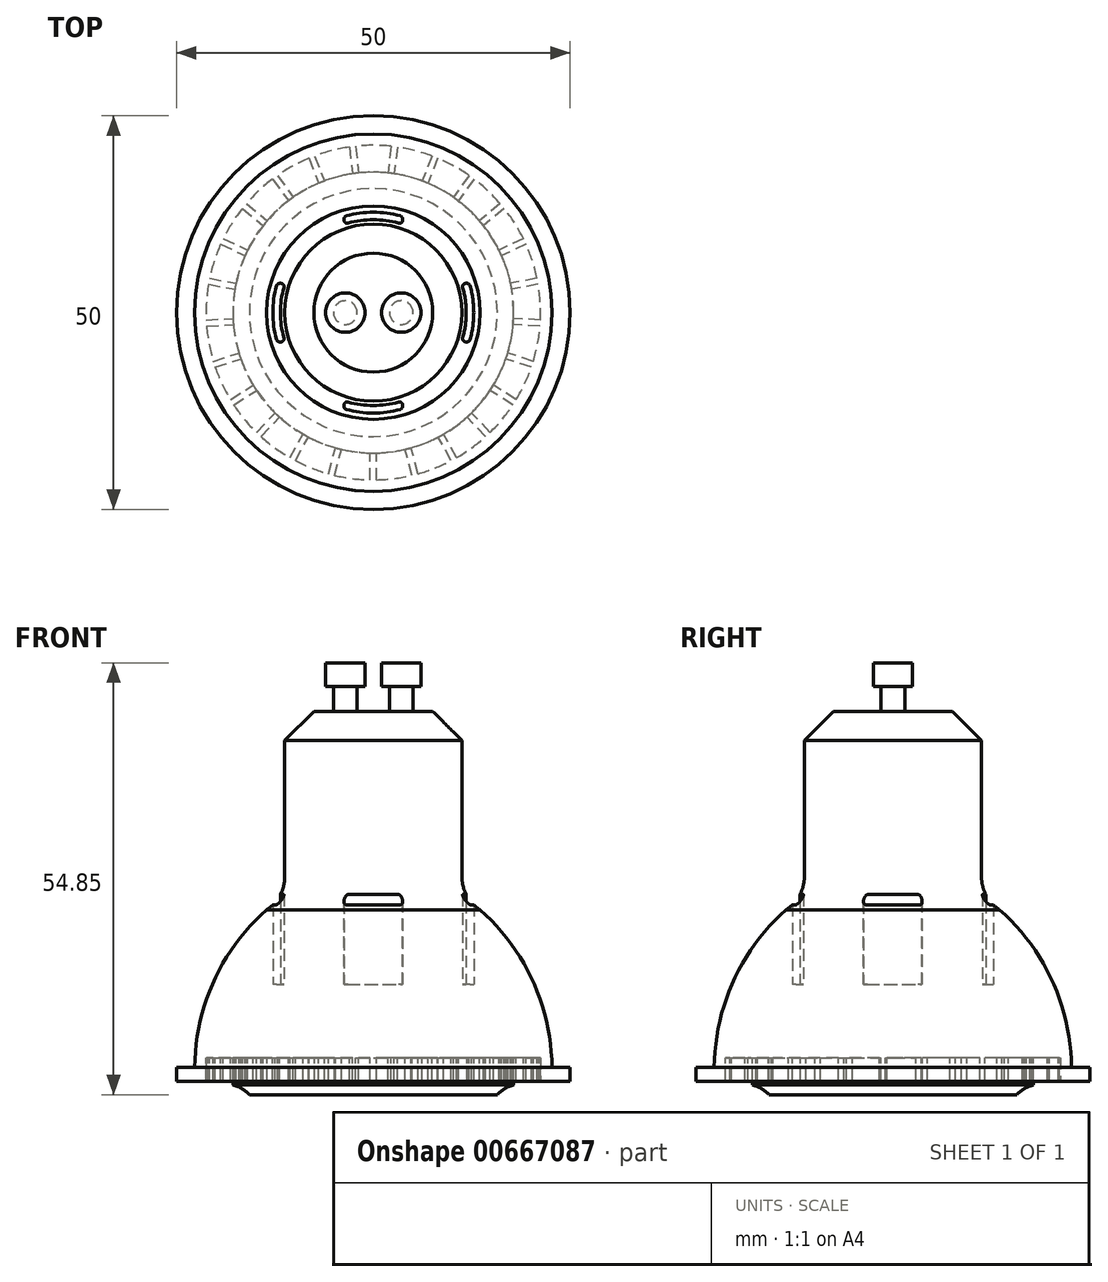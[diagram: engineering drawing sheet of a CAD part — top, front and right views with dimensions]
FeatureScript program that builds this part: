
annotation { "Feature Type Name" : "Feature", "Feature Type Description" : "" }
export const myFeature = defineFeature(function(context is Context, id is Id, definition is map)
    precondition{}
    {
        {
            var Q0;
            Q0=qCreatedBy(makeId("Front.planeOp"),FACE);
            var sketch = newSketch(context, id + "F0", { "sketchPlane" : qUnion([Q0])});
            skLineSegment(sketch, "E0", {"start": v(0, 34.68) * mm, "end": v(0, -12.32) * mm});
            skLineSegment(sketch, "E1", {"start": v(0, -12.32) * mm, "end": v(-25, -12.32) * mm});
            skLineSegment(sketch, "E2", {"start": v(-25, -12.32) * mm, "end": v(-25, -10.52) * mm});
            skLineSegment(sketch, "E3", {"start": v(-25, -10.52) * mm, "end": v(-22.7, -10.52) * mm});
            skLineSegment(sketch, "E4", {"start": v(0, 34.68) * mm, "end": v(-7.55, 34.68) * mm});
            skLineSegment(sketch, "E5", {"start": v(-7.55, 34.68) * mm, "end": v(-11.25, 30.98) * mm});
            skLineSegment(sketch, "E6", {"start": v(-11.25, 30.98) * mm, "end": v(-11.25, 13.7) * mm});
            skArc(sketch, "E7", {"start": v(-13.56, 9.48) * mm, "mid": v(-11.86, 11.3) * mm, "end": v(-11.25, 13.7) * mm});
            skArc(sketch, "E8", {"start": v(-13.56, 9.48) * mm, "mid": v(-20.24, 0.44) * mm, "end": v(-22.7, -10.52) * mm});
            skSolve(sketch);
        }
        {
            var Q0;
            Q0=makeQuery(id+"F0.imprint","IMPRINT",FACE,{"disambiguationData":[TD([[makeQuery(id+"F0.imprint","IMPRINT",EDGE,{"derivedFrom":sQuery(id+"F0.wireOp",EDGE,"E0")}),-1.0]])]});
            var Q1;
            Q1=sQuery(id+"F0.wireOp",EDGE,"E0");
            revolve(context, id + "F1", {"entities" : qUnion([Q0]), "axis" : qUnion([Q1]), "revolveType" : RevolveType.FULL});
        }
        {
            var Q0;
            Q0=makeQuery(id+"F1.opRevolve","SWEPT_FACE",FACE,{"disambiguationData":[OSD([sQuery(id+"F0.wireOp",EDGE,"E4")])]});
            var sketch = newSketch(context, id + "F2", { "sketchPlane" : qUnion([Q0])});
            skCircle(sketch, "E9", {"center": v(-3.55, 0) * mm, "radius": 1.5 * mm});
            skLineSegment(sketch, "E10", {"start": v(0, 1.94) * mm, "end": v(0, -1.69) * mm});
            skCircle(sketch, "E11.MirrorC", {"center": v(3.55, 0) * mm, "radius": 1.5 * mm});
            skSolve(sketch);
        }
        {
            var Q0;
            Q0=qSketchRegion(id+"F2",true);
            extrude(context, id + "F3", {"entities" : qUnion([Q0]), "operationType" : NewBodyOperationType.ADD, "depth" : 3.15 * mm, "offsetDistance" : 25 * mm});
        }
        {
            var Q0;
            Q0=makeQuery(id+"F3.opExtrude","CAP_FACE",FACE,{"disambiguationData":[OSD([sQuery(id+"F2.wireOp",EDGE,"E9")])],"isStart":false});
            var sketch = newSketch(context, id + "F4", { "sketchPlane" : qUnion([Q0])});
            skCircle(sketch, "E12", {"center": v(-3.55, 0) * mm, "radius": 2.5 * mm});
            skLineSegment(sketch, "E13", {"start": v(0, 3.4) * mm, "end": v(0, -2.9) * mm});
            skCircle(sketch, "E14.MirrorC", {"center": v(3.55, 0) * mm, "radius": 2.5 * mm});
            skSolve(sketch);
        }
        {
            var Q0;
            Q0=qSketchRegion(id+"F4",true);
            extrude(context, id + "F5", {"entities" : qUnion([Q0]), "operationType" : NewBodyOperationType.ADD, "depth" : 3 * mm, "offsetDistance" : 25 * mm});
        }
        {
            var Q0;
            Q0=qCreatedBy(makeId("Front.planeOp"),FACE);
            var sketch = newSketch(context, id + "F6", { "sketchPlane" : qUnion([Q0])});
            skLineSegment(sketch, "E15", {"start": v(0, -12.32) * mm, "end": v(0, -14.02) * mm});
            skLineSegment(sketch, "E16", {"start": v(0, -14.02) * mm, "end": v(-15.75, -14.02) * mm});
            skArc(sketch, "E17", {"start": v(-15.75, -14.02) * mm, "mid": v(-16.7, -13.24) * mm, "end": v(-17.84, -12.8) * mm});
            skLineSegment(sketch, "E18", {"start": v(-17.84, -12.8) * mm, "end": v(-17.84, -12.32) * mm});
            skLineSegment(sketch, "E19", {"start": v(-17.84, -12.32) * mm, "end": v(0, -12.32) * mm});
            skSolve(sketch);
        }
        {
            var Q0;
            Q0=qSketchRegion(id+"F6",true);
            var Q1;
            Q1=sQuery(id+"F6.wireOp",EDGE,"E15");
            revolve(context, id + "F7", {"operationType" : NewBodyOperationType.ADD, "entities" : qUnion([Q0]), "axis" : qUnion([Q1]), "revolveType" : RevolveType.FULL});
        }
        {
            var Q0;
            Q0=makeQuery(id+"F1.opRevolve","SWEPT_FACE",FACE,{"disambiguationData":[OSD([sQuery(id+"F0.wireOp",EDGE,"E1")])]});
            var sketch = newSketch(context, id + "F8", { "sketchPlane" : qUnion([Q0])});
            skCircle(sketch, "E20", {"center": v(0, 0) * mm, "radius": 17.84 * mm});
            skCircle(sketch, "E21", {"center": v(0, 0) * mm, "radius": 21.25 * mm});
            skSolve(sketch);
        }
        {
            var Q0;
            Q0=qSketchRegion(id+"F8",true);
            extrude(context, id + "F9", {"entities" : qUnion([Q0]), "operationType" : NewBodyOperationType.REMOVE, "oppositeDirection" : true, "depth" : 3 * mm, "offsetDistance" : 25 * mm});
        }
        {
            var Q0;
            Q0=makeQuery(id+"F9.boolean.opBoolean","COPY",FACE,{"derivedFrom":makeQuery(id+"F9.opExtrude","CAP_FACE",FACE,{"disambiguationData":[OSD([sQuery(id+"F8.wireOp",EDGE,"E20"),sQuery(id+"F8.wireOp",EDGE,"E21")])],"isStart":false})});
            var sketch = newSketch(context, id + "F10", { "sketchPlane" : qUnion([Q0])});
            skLineSegment(sketch, "E22.left", {"start": v(-0.4, 21.25) * mm, "end": v(-0.4, 17.83) * mm});
            skLineSegment(sketch, "E22.right", {"start": v(0.4, 21.25) * mm, "end": v(0.4, 17.83) * mm});
            skArc(sketch, "E23", {"start": v(0.4, 17.83) * mm, "mid": v(0, 17.84) * mm, "end": v(-0.39, 17.83) * mm});
            skArc(sketch, "E24", {"start": v(0.39, 21.25) * mm, "mid": v(0, 21.25) * mm, "end": v(-0.39, 21.25) * mm});
            skArc(sketch, "E25.1.0", {"start": v(-4.9, 20.68) * mm, "mid": v(-5.28, 20.58) * mm, "end": v(-5.66, 20.48) * mm});
            skLineSegment(sketch, "E25.1.1", {"start": v(-4.9, 20.68) * mm, "end": v(-4.06, 17.37) * mm});
            skLineSegment(sketch, "E25.1.2", {"start": v(-5.66, 20.48) * mm, "end": v(-4.81, 17.17) * mm});
            skArc(sketch, "E25.1.3", {"start": v(-4.06, 17.37) * mm, "mid": v(-4.44, 17.28) * mm, "end": v(-4.81, 17.17) * mm});
            skArc(sketch, "E25.2.0", {"start": v(-9.9, 18.8) * mm, "mid": v(-10.24, 18.62) * mm, "end": v(-10.58, 18.43) * mm});
            skLineSegment(sketch, "E25.2.1", {"start": v(-9.9, 18.8) * mm, "end": v(-8.25, 15.81) * mm});
            skLineSegment(sketch, "E25.2.2", {"start": v(-10.58, 18.43) * mm, "end": v(-8.93, 15.44) * mm});
            skArc(sketch, "E25.2.3", {"start": v(-8.25, 15.81) * mm, "mid": v(-8.6, 15.63) * mm, "end": v(-8.93, 15.44) * mm});
            skArc(sketch, "E26.3.3.0", {"start": v(-14.26, 15.75) * mm, "mid": v(-14.55, 15.5) * mm, "end": v(-14.83, 15.22) * mm});
            skLineSegment(sketch, "E26.4.3.0", {"start": v(-14.26, 15.75) * mm, "end": v(-11.92, 13.27) * mm});
            skLineSegment(sketch, "E26.7.3.0", {"start": v(-14.83, 15.22) * mm, "end": v(-12.5, 12.73) * mm});
            skArc(sketch, "E26.10.3.0", {"start": v(-11.92, 13.27) * mm, "mid": v(-12.2, 13) * mm, "end": v(-12.5, 12.73) * mm});
            skArc(sketch, "E26.3.4.0", {"start": v(-17.73, 11.71) * mm, "mid": v(-17.94, 11.39) * mm, "end": v(-18.15, 11.06) * mm});
            skLineSegment(sketch, "E26.4.4.0", {"start": v(-17.73, 11.71) * mm, "end": v(-14.85, 9.88) * mm});
            skLineSegment(sketch, "E26.7.4.0", {"start": v(-18.15, 11.06) * mm, "end": v(-15.27, 9.23) * mm});
            skArc(sketch, "E26.10.4.0", {"start": v(-14.85, 9.88) * mm, "mid": v(-15.06, 9.56) * mm, "end": v(-15.27, 9.23) * mm});
            skArc(sketch, "E26.3.5.0", {"start": v(-20.09, 6.94) * mm, "mid": v(-20.2, 6.57) * mm, "end": v(-20.33, 6.2) * mm});
            skLineSegment(sketch, "E26.4.5.0", {"start": v(-20.09, 6.94) * mm, "end": v(-16.84, 5.88) * mm});
            skLineSegment(sketch, "E26.7.5.0", {"start": v(-20.33, 6.2) * mm, "end": v(-17.08, 5.14) * mm});
            skArc(sketch, "E26.10.5.0", {"start": v(-16.84, 5.88) * mm, "mid": v(-16.96, 5.51) * mm, "end": v(-17.08, 5.14) * mm});
            skArc(sketch, "E26.3.6.0", {"start": v(-21.18, 1.72) * mm, "mid": v(-21.2, 1.33) * mm, "end": v(-21.23, 0.94) * mm});
            skLineSegment(sketch, "E26.4.6.0", {"start": v(-21.18, 1.72) * mm, "end": v(-17.77, 1.5) * mm});
            skLineSegment(sketch, "E26.7.6.0", {"start": v(-21.23, 0.94) * mm, "end": v(-17.82, 0.73) * mm});
            skArc(sketch, "E26.10.6.0", {"start": v(-17.77, 1.5) * mm, "mid": v(-17.8, 1.12) * mm, "end": v(-17.82, 0.73) * mm});
            skArc(sketch, "E26.3.7.0", {"start": v(-20.94, -3.6) * mm, "mid": v(-20.87, -3.98) * mm, "end": v(-20.8, -4.36) * mm});
            skLineSegment(sketch, "E26.4.7.0", {"start": v(-20.94, -3.6) * mm, "end": v(-17.59, -2.96) * mm});
            skLineSegment(sketch, "E26.7.7.0", {"start": v(-20.8, -4.36) * mm, "end": v(-17.44, -3.72) * mm});
            skArc(sketch, "E26.10.7.0", {"start": v(-17.59, -2.96) * mm, "mid": v(-17.52, -3.34) * mm, "end": v(-17.44, -3.72) * mm});
            skArc(sketch, "E26.3.8.0", {"start": v(-19.4, -8.7) * mm, "mid": v(-19.23, -9.05) * mm, "end": v(-19.06, -9.4) * mm});
            skLineSegment(sketch, "E26.4.8.0", {"start": v(-19.4, -8.7) * mm, "end": v(-16.3, -7.24) * mm});
            skLineSegment(sketch, "E26.7.8.0", {"start": v(-19.06, -9.4) * mm, "end": v(-15.97, -7.95) * mm});
            skArc(sketch, "E26.10.8.0", {"start": v(-16.3, -7.24) * mm, "mid": v(-16.14, -7.6) * mm, "end": v(-15.97, -7.95) * mm});
            skArc(sketch, "E26.3.9.0", {"start": v(-16.62, -13.24) * mm, "mid": v(-16.37, -13.55) * mm, "end": v(-16.12, -13.84) * mm});
            skLineSegment(sketch, "E26.4.9.0", {"start": v(-16.62, -13.24) * mm, "end": v(-13.99, -11.07) * mm});
            skLineSegment(sketch, "E26.7.9.0", {"start": v(-16.12, -13.84) * mm, "end": v(-13.5, -11.67) * mm});
            skArc(sketch, "E26.10.9.0", {"start": v(-13.99, -11.07) * mm, "mid": v(-13.74, -11.37) * mm, "end": v(-13.5, -11.67) * mm});
            skArc(sketch, "E26.3.10.0", {"start": v(-12.8, -16.96) * mm, "mid": v(-12.5, -17.2) * mm, "end": v(-12.17, -17.42) * mm});
            skLineSegment(sketch, "E26.4.10.0", {"start": v(-12.8, -16.96) * mm, "end": v(-10.8, -14.2) * mm});
            skLineSegment(sketch, "E26.7.10.0", {"start": v(-12.17, -17.42) * mm, "end": v(-10.17, -14.66) * mm});
            skArc(sketch, "E26.10.10.0", {"start": v(-10.8, -14.2) * mm, "mid": v(-10.48, -14.43) * mm, "end": v(-10.17, -14.66) * mm});
            skArc(sketch, "E26.3.11.0", {"start": v(-8.18, -19.61) * mm, "mid": v(-7.82, -19.76) * mm, "end": v(-7.46, -19.9) * mm});
            skLineSegment(sketch, "E26.4.11.0", {"start": v(-8.18, -19.61) * mm, "end": v(-6.93, -16.44) * mm});
            skLineSegment(sketch, "E26.7.11.0", {"start": v(-7.46, -19.9) * mm, "end": v(-6.2, -16.72) * mm});
            skArc(sketch, "E26.10.11.0", {"start": v(-6.93, -16.44) * mm, "mid": v(-6.57, -16.58) * mm, "end": v(-6.2, -16.72) * mm});
            skArc(sketch, "E26.3.12.0", {"start": v(-3.05, -21.03) * mm, "mid": v(-2.66, -21.08) * mm, "end": v(-2.28, -21.13) * mm});
            skLineSegment(sketch, "E26.4.12.0", {"start": v(-3.05, -21.03) * mm, "end": v(-2.62, -17.64) * mm});
            skLineSegment(sketch, "E26.7.12.0", {"start": v(-2.28, -21.13) * mm, "end": v(-1.85, -17.74) * mm});
            skArc(sketch, "E26.10.12.0", {"start": v(-2.62, -17.64) * mm, "mid": v(-2.24, -17.7) * mm, "end": v(-1.85, -17.74) * mm});
            skArc(sketch, "E26.3.13.0", {"start": v(2.28, -21.13) * mm, "mid": v(2.66, -21.08) * mm, "end": v(3.05, -21.03) * mm});
            skLineSegment(sketch, "E26.4.13.0", {"start": v(2.28, -21.13) * mm, "end": v(1.85, -17.74) * mm});
            skLineSegment(sketch, "E26.7.13.0", {"start": v(3.05, -21.03) * mm, "end": v(2.62, -17.64) * mm});
            skArc(sketch, "E26.10.13.0", {"start": v(1.85, -17.74) * mm, "mid": v(2.24, -17.7) * mm, "end": v(2.62, -17.64) * mm});
            skArc(sketch, "E26.3.14.0", {"start": v(7.46, -19.9) * mm, "mid": v(7.82, -19.76) * mm, "end": v(8.18, -19.61) * mm});
            skLineSegment(sketch, "E26.4.14.0", {"start": v(7.46, -19.9) * mm, "end": v(6.2, -16.72) * mm});
            skLineSegment(sketch, "E26.7.14.0", {"start": v(8.18, -19.61) * mm, "end": v(6.93, -16.44) * mm});
            skArc(sketch, "E26.10.14.0", {"start": v(6.2, -16.72) * mm, "mid": v(6.57, -16.58) * mm, "end": v(6.93, -16.44) * mm});
            skArc(sketch, "E26.3.15.0", {"start": v(12.17, -17.42) * mm, "mid": v(12.5, -17.2) * mm, "end": v(12.8, -16.96) * mm});
            skLineSegment(sketch, "E26.4.15.0", {"start": v(12.17, -17.42) * mm, "end": v(10.17, -14.66) * mm});
            skLineSegment(sketch, "E26.7.15.0", {"start": v(12.8, -16.96) * mm, "end": v(10.8, -14.2) * mm});
            skArc(sketch, "E26.10.15.0", {"start": v(10.17, -14.66) * mm, "mid": v(10.48, -14.43) * mm, "end": v(10.8, -14.2) * mm});
            skArc(sketch, "E26.3.16.0", {"start": v(16.12, -13.84) * mm, "mid": v(16.37, -13.55) * mm, "end": v(16.62, -13.24) * mm});
            skLineSegment(sketch, "E26.4.16.0", {"start": v(16.12, -13.84) * mm, "end": v(13.5, -11.67) * mm});
            skLineSegment(sketch, "E26.7.16.0", {"start": v(16.62, -13.24) * mm, "end": v(13.99, -11.07) * mm});
            skArc(sketch, "E26.10.16.0", {"start": v(13.5, -11.67) * mm, "mid": v(13.74, -11.37) * mm, "end": v(13.99, -11.07) * mm});
            skArc(sketch, "E26.3.17.0", {"start": v(19.06, -9.4) * mm, "mid": v(19.23, -9.05) * mm, "end": v(19.4, -8.7) * mm});
            skLineSegment(sketch, "E26.4.17.0", {"start": v(19.06, -9.4) * mm, "end": v(15.97, -7.95) * mm});
            skLineSegment(sketch, "E26.7.17.0", {"start": v(19.4, -8.7) * mm, "end": v(16.3, -7.24) * mm});
            skArc(sketch, "E26.10.17.0", {"start": v(15.97, -7.95) * mm, "mid": v(16.14, -7.6) * mm, "end": v(16.3, -7.24) * mm});
            skArc(sketch, "E26.3.18.0", {"start": v(20.8, -4.36) * mm, "mid": v(20.87, -3.98) * mm, "end": v(20.94, -3.6) * mm});
            skLineSegment(sketch, "E26.4.18.0", {"start": v(20.8, -4.36) * mm, "end": v(17.44, -3.72) * mm});
            skLineSegment(sketch, "E26.7.18.0", {"start": v(20.94, -3.6) * mm, "end": v(17.59, -2.96) * mm});
            skArc(sketch, "E26.10.18.0", {"start": v(17.44, -3.72) * mm, "mid": v(17.52, -3.34) * mm, "end": v(17.59, -2.96) * mm});
            skArc(sketch, "E26.3.19.0", {"start": v(21.23, 0.94) * mm, "mid": v(21.2, 1.33) * mm, "end": v(21.18, 1.72) * mm});
            skLineSegment(sketch, "E26.4.19.0", {"start": v(21.23, 0.94) * mm, "end": v(17.82, 0.73) * mm});
            skLineSegment(sketch, "E26.7.19.0", {"start": v(21.18, 1.72) * mm, "end": v(17.77, 1.5) * mm});
            skArc(sketch, "E26.10.19.0", {"start": v(17.82, 0.73) * mm, "mid": v(17.8, 1.12) * mm, "end": v(17.77, 1.5) * mm});
            skArc(sketch, "E26.3.20.0", {"start": v(20.33, 6.2) * mm, "mid": v(20.2, 6.57) * mm, "end": v(20.09, 6.94) * mm});
            skLineSegment(sketch, "E26.4.20.0", {"start": v(20.33, 6.2) * mm, "end": v(17.08, 5.14) * mm});
            skLineSegment(sketch, "E26.7.20.0", {"start": v(20.09, 6.94) * mm, "end": v(16.84, 5.88) * mm});
            skArc(sketch, "E26.10.20.0", {"start": v(17.08, 5.14) * mm, "mid": v(16.96, 5.51) * mm, "end": v(16.84, 5.88) * mm});
            skArc(sketch, "E26.3.21.0", {"start": v(18.15, 11.06) * mm, "mid": v(17.94, 11.39) * mm, "end": v(17.73, 11.71) * mm});
            skLineSegment(sketch, "E26.4.21.0", {"start": v(18.15, 11.06) * mm, "end": v(15.27, 9.23) * mm});
            skLineSegment(sketch, "E26.7.21.0", {"start": v(17.73, 11.71) * mm, "end": v(14.85, 9.88) * mm});
            skArc(sketch, "E26.10.21.0", {"start": v(15.27, 9.23) * mm, "mid": v(15.06, 9.56) * mm, "end": v(14.85, 9.88) * mm});
            skArc(sketch, "E26.3.22.0", {"start": v(14.83, 15.22) * mm, "mid": v(14.55, 15.5) * mm, "end": v(14.26, 15.75) * mm});
            skLineSegment(sketch, "E26.4.22.0", {"start": v(14.83, 15.22) * mm, "end": v(12.5, 12.73) * mm});
            skLineSegment(sketch, "E26.7.22.0", {"start": v(14.26, 15.75) * mm, "end": v(11.92, 13.27) * mm});
            skArc(sketch, "E26.10.22.0", {"start": v(12.5, 12.73) * mm, "mid": v(12.2, 13) * mm, "end": v(11.92, 13.27) * mm});
            skArc(sketch, "E26.3.23.0", {"start": v(10.58, 18.43) * mm, "mid": v(10.24, 18.62) * mm, "end": v(9.9, 18.8) * mm});
            skLineSegment(sketch, "E26.4.23.0", {"start": v(10.58, 18.43) * mm, "end": v(8.93, 15.44) * mm});
            skLineSegment(sketch, "E26.7.23.0", {"start": v(9.9, 18.8) * mm, "end": v(8.25, 15.81) * mm});
            skArc(sketch, "E26.10.23.0", {"start": v(8.93, 15.44) * mm, "mid": v(8.6, 15.63) * mm, "end": v(8.25, 15.81) * mm});
            skArc(sketch, "E26.3.24.0", {"start": v(5.66, 20.48) * mm, "mid": v(5.28, 20.58) * mm, "end": v(4.9, 20.68) * mm});
            skLineSegment(sketch, "E26.4.24.0", {"start": v(5.66, 20.48) * mm, "end": v(4.81, 17.17) * mm});
            skLineSegment(sketch, "E26.7.24.0", {"start": v(4.9, 20.68) * mm, "end": v(4.06, 17.37) * mm});
            skArc(sketch, "E26.10.24.0", {"start": v(4.81, 17.17) * mm, "mid": v(4.44, 17.28) * mm, "end": v(4.06, 17.37) * mm});
            skSolve(sketch);
        }
        {
            var Q0;
            Q0=qSketchRegion(id+"F10",true);
            var Q1;
            Q1=makeQuery(id+"F1.opRevolve","SWEPT_FACE",FACE,{"disambiguationData":[OSD([sQuery(id+"F0.wireOp",EDGE,"E1")])]});
            extrude(context, id + "F11", {"entities" : qUnion([Q0]), "operationType" : NewBodyOperationType.ADD, "endBound" : BoundingType.UP_TO_SURFACE, "depth" : 25 * mm, "endBoundEntityFace" : qUnion([Q1]), "offsetDistance" : 25 * mm});
        }
        {
            var Q0;
            Q0=qCreatedBy(makeId("Top.planeOp"),FACE);
            var sketch = newSketch(context, id + "F12", { "sketchPlane" : qUnion([Q0])});
            skArc(sketch, "E27", {"start": v(3.72, 11.2) * mm, "mid": v(0, 11.8) * mm, "end": v(-3.72, 11.2) * mm});
            skArc(sketch, "E28", {"start": v(3.72, 12.2) * mm, "mid": v(0, 12.76) * mm, "end": v(-3.72, 12.2) * mm});
            skLineSegment(sketch, "E29", {"start": v(-3.72, 12.2) * mm, "end": v(-3.72, 11.2) * mm});
            skLineSegment(sketch, "E30.MirrorCS", {"start": v(3.72, 12.2) * mm, "end": v(3.72, 11.2) * mm});
            skPoint(sketch, "E31.start.orphan", {"position": v(0, 15.57) * mm});
            skArc(sketch, "E32.1.0", {"start": v(-12.2, 3.72) * mm, "mid": v(-12.76, 0) * mm, "end": v(-12.2, -3.72) * mm});
            skLineSegment(sketch, "E32.1.1", {"start": v(-12.2, -3.72) * mm, "end": v(-11.2, -3.72) * mm});
            skArc(sketch, "E32.1.2", {"start": v(-11.2, 3.72) * mm, "mid": v(-11.8, 0) * mm, "end": v(-11.2, -3.72) * mm});
            skLineSegment(sketch, "E32.1.3", {"start": v(-12.2, 3.72) * mm, "end": v(-11.2, 3.72) * mm});
            skArc(sketch, "E32.2.0", {"start": v(-3.72, -12.2) * mm, "mid": v(0, -12.76) * mm, "end": v(3.72, -12.2) * mm});
            skLineSegment(sketch, "E32.2.1", {"start": v(3.72, -12.2) * mm, "end": v(3.72, -11.2) * mm});
            skArc(sketch, "E32.2.2", {"start": v(-3.72, -11.2) * mm, "mid": v(0, -11.8) * mm, "end": v(3.72, -11.2) * mm});
            skLineSegment(sketch, "E32.2.3", {"start": v(-3.72, -12.2) * mm, "end": v(-3.72, -11.2) * mm});
            skArc(sketch, "E32.3.0", {"start": v(12.2, -3.72) * mm, "mid": v(12.76, 0) * mm, "end": v(12.2, 3.72) * mm});
            skLineSegment(sketch, "E32.3.1", {"start": v(12.2, 3.72) * mm, "end": v(11.2, 3.72) * mm});
            skArc(sketch, "E32.3.2", {"start": v(11.2, -3.72) * mm, "mid": v(11.8, 0) * mm, "end": v(11.2, 3.72) * mm});
            skLineSegment(sketch, "E32.3.3", {"start": v(12.2, -3.72) * mm, "end": v(11.2, -3.72) * mm});
            skSolve(sketch);
        }
        {
            var Q0;
            Q0=qSketchRegion(id+"F12",true);
            extrude(context, id + "F13", {"entities" : qUnion([Q0]), "operationType" : NewBodyOperationType.REMOVE, "depth" : 22.5 * mm, "offsetDistance" : 25 * mm});
        }
        {
            var Q0;
            Q0=makeQuery(id+"F13.boolean.opBoolean","COPY",EDGE,{"derivedFrom":makeQuery(id+"F13.opExtrude","SWEPT_EDGE",EDGE,{"disambiguationData":[OSD([sQuery(id+"F12.wireOp",EDGE,"E27"),sQuery(id+"F12.wireOp",EDGE,"E29")])]})});
            var Q1;
            Q1=makeQuery(id+"F13.boolean.opBoolean","COPY",EDGE,{"derivedFrom":makeQuery(id+"F13.opExtrude","SWEPT_EDGE",EDGE,{"disambiguationData":[OSD([sQuery(id+"F12.wireOp",EDGE,"E28"),sQuery(id+"F12.wireOp",EDGE,"E29")])]})});
            var Q2;
            Q2=makeQuery(id+"F13.boolean.opBoolean","COPY",EDGE,{"derivedFrom":makeQuery(id+"F13.opExtrude","SWEPT_EDGE",EDGE,{"disambiguationData":[OSD([sQuery(id+"F12.wireOp",EDGE,"E27"),sQuery(id+"F12.wireOp",EDGE,"E30.MirrorCS")])]})});
            var Q3;
            Q3=makeQuery(id+"F13.boolean.opBoolean","COPY",EDGE,{"derivedFrom":makeQuery(id+"F13.opExtrude","SWEPT_EDGE",EDGE,{"disambiguationData":[OSD([sQuery(id+"F12.wireOp",EDGE,"E28"),sQuery(id+"F12.wireOp",EDGE,"E30.MirrorCS")])]})});
            var Q4;
            Q4=makeQuery(id+"F13.boolean.opBoolean","COPY",EDGE,{"derivedFrom":makeQuery(id+"F13.opExtrude","SWEPT_EDGE",EDGE,{"disambiguationData":[OSD([sQuery(id+"F12.wireOp",EDGE,"E32.1.0"),sQuery(id+"F12.wireOp",EDGE,"E32.1.3")])]})});
            var Q5;
            Q5=makeQuery(id+"F13.boolean.opBoolean","COPY",EDGE,{"derivedFrom":makeQuery(id+"F13.opExtrude","SWEPT_EDGE",EDGE,{"disambiguationData":[OSD([sQuery(id+"F12.wireOp",EDGE,"E32.1.2"),sQuery(id+"F12.wireOp",EDGE,"E32.1.3")])]})});
            var Q6;
            Q6=makeQuery(id+"F13.boolean.opBoolean","COPY",EDGE,{"derivedFrom":makeQuery(id+"F13.opExtrude","SWEPT_EDGE",EDGE,{"disambiguationData":[OSD([sQuery(id+"F12.wireOp",EDGE,"E32.1.1"),sQuery(id+"F12.wireOp",EDGE,"E32.1.2")])]})});
            var Q7;
            Q7=makeQuery(id+"F13.boolean.opBoolean","COPY",EDGE,{"derivedFrom":makeQuery(id+"F13.opExtrude","SWEPT_EDGE",EDGE,{"disambiguationData":[OSD([sQuery(id+"F12.wireOp",EDGE,"E32.1.0"),sQuery(id+"F12.wireOp",EDGE,"E32.1.1")])]})});
            var Q8;
            Q8=makeQuery(id+"F13.boolean.opBoolean","COPY",EDGE,{"derivedFrom":makeQuery(id+"F13.opExtrude","SWEPT_EDGE",EDGE,{"disambiguationData":[OSD([sQuery(id+"F12.wireOp",EDGE,"E32.3.1"),sQuery(id+"F12.wireOp",EDGE,"E32.3.2")])]})});
            var Q9;
            Q9=makeQuery(id+"F13.boolean.opBoolean","COPY",EDGE,{"derivedFrom":makeQuery(id+"F13.opExtrude","SWEPT_EDGE",EDGE,{"disambiguationData":[OSD([sQuery(id+"F12.wireOp",EDGE,"E32.3.2"),sQuery(id+"F12.wireOp",EDGE,"E32.3.3")])]})});
            var Q10;
            Q10=makeQuery(id+"F13.boolean.opBoolean","COPY",EDGE,{"derivedFrom":makeQuery(id+"F13.opExtrude","SWEPT_EDGE",EDGE,{"disambiguationData":[OSD([sQuery(id+"F12.wireOp",EDGE,"E32.3.0"),sQuery(id+"F12.wireOp",EDGE,"E32.3.3")])]})});
            var Q11;
            Q11=makeQuery(id+"F13.boolean.opBoolean","COPY",EDGE,{"derivedFrom":makeQuery(id+"F13.opExtrude","SWEPT_EDGE",EDGE,{"disambiguationData":[OSD([sQuery(id+"F12.wireOp",EDGE,"E32.3.0"),sQuery(id+"F12.wireOp",EDGE,"E32.3.1")])]})});
            var Q12;
            Q12=makeQuery(id+"F13.boolean.opBoolean","COPY",EDGE,{"derivedFrom":makeQuery(id+"F13.opExtrude","SWEPT_EDGE",EDGE,{"disambiguationData":[OSD([sQuery(id+"F12.wireOp",EDGE,"E32.2.0"),sQuery(id+"F12.wireOp",EDGE,"E32.2.3")])]})});
            var Q13;
            Q13=makeQuery(id+"F13.boolean.opBoolean","COPY",EDGE,{"derivedFrom":makeQuery(id+"F13.opExtrude","SWEPT_EDGE",EDGE,{"disambiguationData":[OSD([sQuery(id+"F12.wireOp",EDGE,"E32.2.2"),sQuery(id+"F12.wireOp",EDGE,"E32.2.3")])]})});
            var Q14;
            Q14=makeQuery(id+"F13.boolean.opBoolean","COPY",EDGE,{"derivedFrom":makeQuery(id+"F13.opExtrude","SWEPT_EDGE",EDGE,{"disambiguationData":[OSD([sQuery(id+"F12.wireOp",EDGE,"E32.2.1"),sQuery(id+"F12.wireOp",EDGE,"E32.2.2")])]})});
            var Q15;
            Q15=makeQuery(id+"F13.boolean.opBoolean","COPY",EDGE,{"derivedFrom":makeQuery(id+"F13.opExtrude","SWEPT_EDGE",EDGE,{"disambiguationData":[OSD([sQuery(id+"F12.wireOp",EDGE,"E32.2.0"),sQuery(id+"F12.wireOp",EDGE,"E32.2.1")])]})});
            fillet(context, id + "F14", {"entities" : qUnion([Q0, Q1, Q2, Q3, Q4, Q5, Q6, Q7, Q8, Q9, Q10, Q11, Q12, Q13, Q14, Q15]), "radius" : 0.4 * mm, "tangentPropagation" : true, "allowEdgeOverflow" : false});
        }
    });
